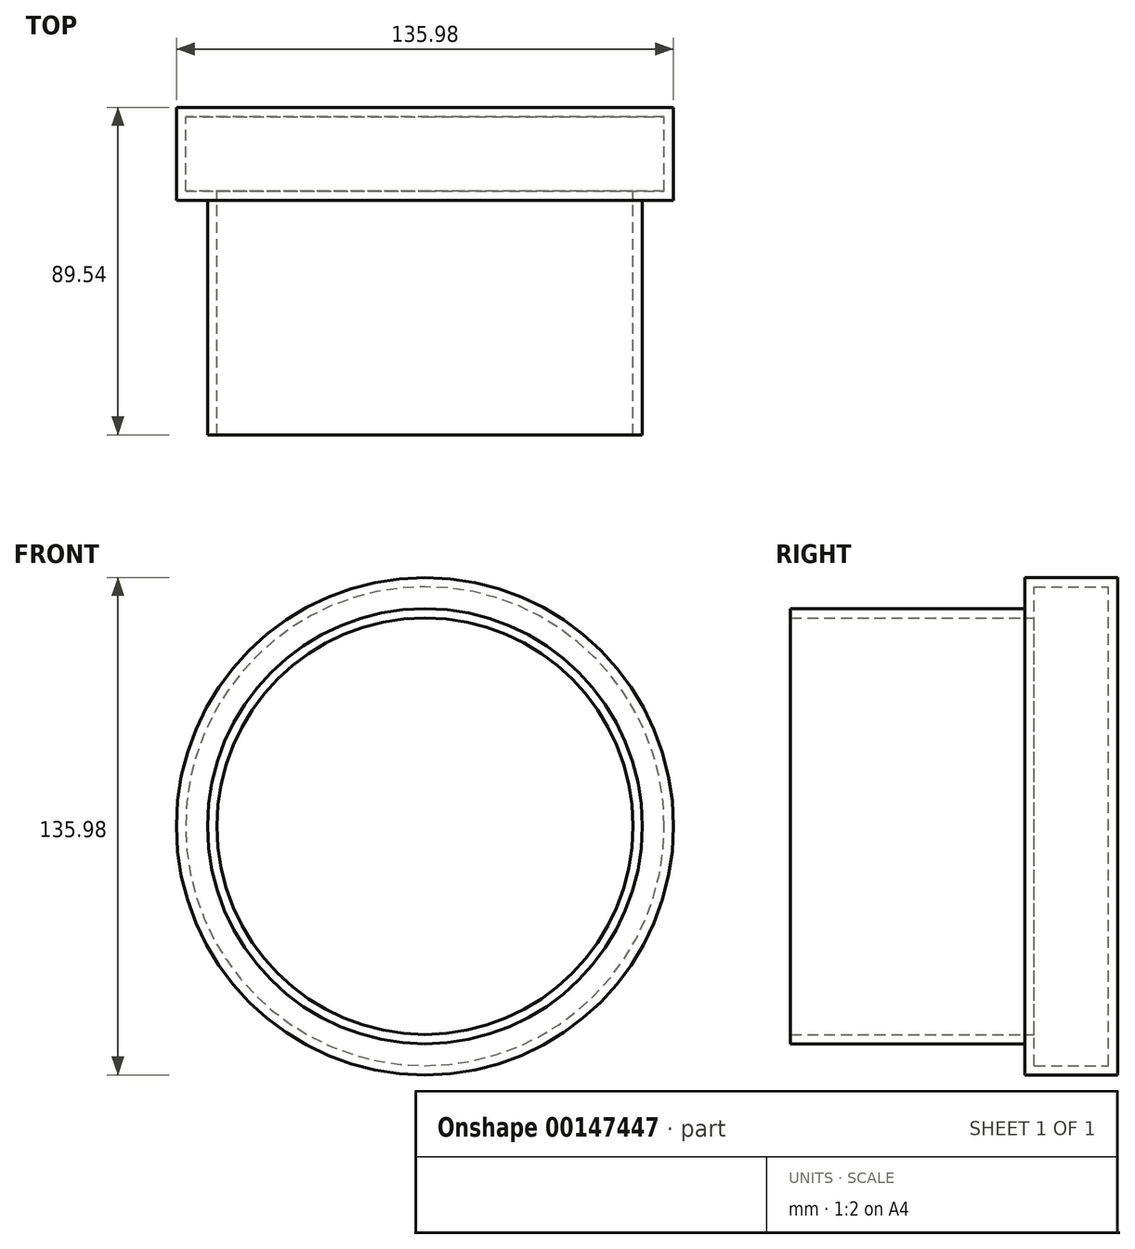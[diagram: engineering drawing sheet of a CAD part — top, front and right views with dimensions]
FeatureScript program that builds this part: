
annotation { "Feature Type Name" : "Feature", "Feature Type Description" : "" }
export const myFeature = defineFeature(function(context is Context, id is Id, definition is map)
    precondition{}
    {
        {
            var Q0;
            Q0=qCreatedBy(makeId("Front.planeOp"),FACE);
            var sketch = newSketch(context, id + "F0", { "sketchPlane" : qUnion([Q0])});
            skCircle(sketch, "E0", {"center": v(0, 0) * mm, "radius": 68 * mm});
            skSolve(sketch);
        }
        {
            var Q0;
            Q0 = qSketchRegion(id + "F0", true);
            extrude(context, id + "F1", {"entities" : qUnion([Q0]), "depth" : 25.4 * mm});
        }
        {
            var Q0;
            Q0=qCreatedBy(makeId("Front.planeOp"),FACE);
            var sketch = newSketch(context, id + "F2", { "sketchPlane" : qUnion([Q0])});
            skCircle(sketch, "E1", {"center": v(0, 0) * mm, "radius": 59.47 * mm});
            skSolve(sketch);
        }
        {
            var Q0;
            Q0 = qSketchRegion(id + "F2", true);
            extrude(context, id + "F3", {"entities" : qUnion([Q0]), "operationType" : NewBodyOperationType.ADD, "depth" : 89.53 * mm});
        }
        {
            var Q0;
            Q0=makeQuery(id+"F3.opExtrude","CAP_FACE",FACE,{"disambiguationData":[OSD([sQuery(id+"F2.wireOp",EDGE,"E1")])],"isStart":false});
            shell(context, id + "F4", {"entities" : qUnion([Q0]), "thickness" : 2.54 * mm});
        }
    });
